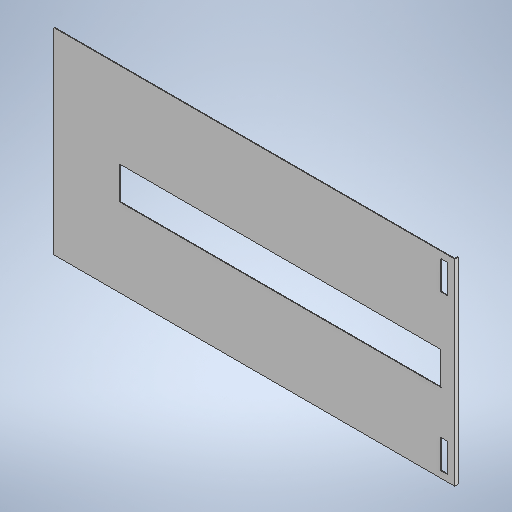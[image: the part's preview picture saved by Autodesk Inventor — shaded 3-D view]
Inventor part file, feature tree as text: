
AUTODESK INVENTOR PART (.ipt)
format: ipt  version: 2025.1 (Build 291241020, 241B)  size: 247,808 bytes
history: native  units: in
note: dims shown in document units (in); Inventor stores cm internally (conversion verified against a paired STEP export)
features: extrude x4, sketch x4
ambient origin geometry x8: Origin, YZ Plane, XZ Plane, XY Plane, X Axis, Y Axis, Z Axis, Center Point
bodies: Solid1 (feature_tree)
feature tree (8):
  extrude  "Extrusion1"  Depth=6.1in
  extrude  "Extrusion2"  Depth=0.438in
  extrude  "Extrusion3"  Depth=0.1in
  extrude  "Extrusion4"  Depth=0.1in
  sketch  "Sketch1"  dims[d0=3.0in d1=6.1in]
  sketch  "Sketch2"  dims[d2=0.01in d3=0.0in d4=0.438in]
  sketch  "Sketch3"  dims[d5=0.1in d6=0.1in]
  sketch  "Sketch4"  dims[d7=0.1in d8=0.1in d9=0.438in d10=1.0in d11=0.0in d12=0.05in d13=0.01in d14=0.0in d15=0.5in d16=0.0in d17=1.3in d18=1.0in d19=1.0in d20=0.0in]
